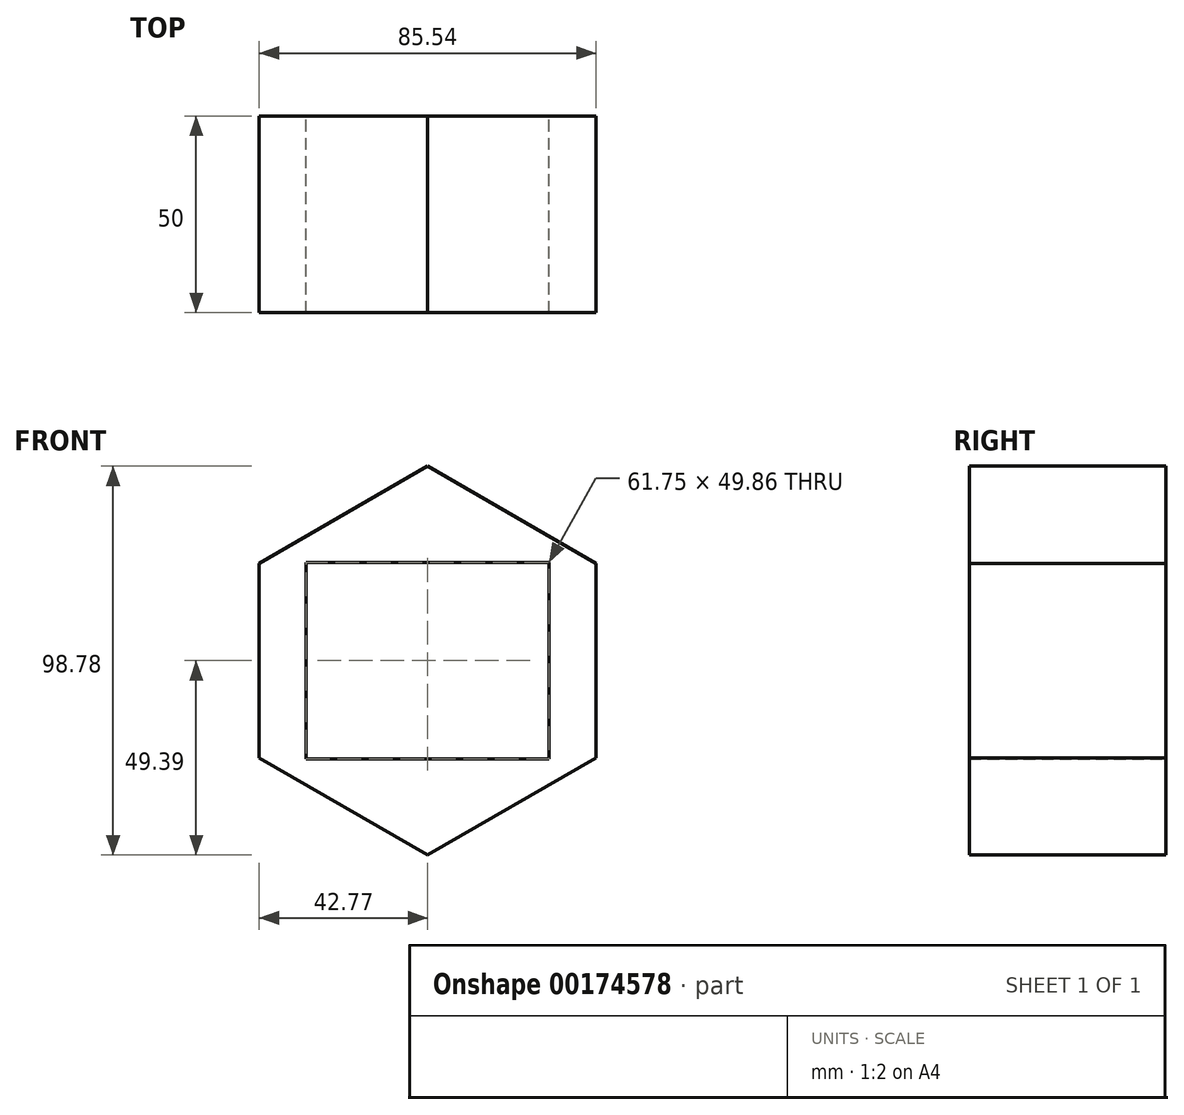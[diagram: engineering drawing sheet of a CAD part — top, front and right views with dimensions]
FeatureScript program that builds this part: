
annotation { "Feature Type Name" : "Feature", "Feature Type Description" : "" }
export const myFeature = defineFeature(function(context is Context, id is Id, definition is map)
    precondition{}
    {
        {
            var Q0;
            Q0=qCreatedBy(makeId("Front.planeOp"),FACE);
            var sketch = newSketch(context, id + "F0", { "sketchPlane" : qUnion([Q0])});
            skCircle(sketch, "E0.cCircle", {"center": v(0, 0) * mm, "radius": 42.77 * mm, "construction": true});
            skLineSegment(sketch, "E0.0", {"start": v(-42.77, -24.7) * mm, "end": v(-42.77, 24.7) * mm});
            skLineSegment(sketch, "E0.1", {"start": v(-42.77, 24.7) * mm, "end": v(0, 49.4) * mm});
            skLineSegment(sketch, "E0.2", {"start": v(0, 49.4) * mm, "end": v(42.77, 24.7) * mm});
            skLineSegment(sketch, "E0.3", {"start": v(42.77, 24.7) * mm, "end": v(42.77, -24.7) * mm});
            skLineSegment(sketch, "E0.4", {"start": v(42.77, -24.7) * mm, "end": v(0, -49.4) * mm});
            skLineSegment(sketch, "E0.5", {"start": v(0, -49.4) * mm, "end": v(-42.77, -24.7) * mm});
            skPoint(sketch, "E0.0.midPoint", {"position": v(-42.77, 0) * mm});
            skCircle(sketch, "E1", {"center": v(0, 0) * mm, "radius": 10 * mm});
            skLineSegment(sketch, "E2.bottom", {"start": v(-30.88, -24.93) * mm, "end": v(30.88, -24.93) * mm});
            skLineSegment(sketch, "E2.top", {"start": v(-30.88, 24.93) * mm, "end": v(30.88, 24.93) * mm});
            skLineSegment(sketch, "E2.left", {"start": v(-30.88, -24.93) * mm, "end": v(-30.88, 24.93) * mm});
            skLineSegment(sketch, "E2.right", {"start": v(30.88, -24.93) * mm, "end": v(30.88, 24.93) * mm});
            skArc(sketch, "E3", {"start": v(-17.56, 0) * mm, "mid": v(0, 17.56) * mm, "end": v(17.56, 0) * mm});
            skArc(sketch, "E4", {"start": v(-17.56, 0) * mm, "mid": v(0, -17.56) * mm, "end": v(17.56, 0) * mm});
            skSolve(sketch);
        }
        {
            var Q0;
            Q0=makeQuery(id+"F0.imprint","IMPRINT",FACE,{"disambiguationData":[TD([[makeQuery(id+"F0.imprint","IMPRINT",EDGE,{"derivedFrom":sQuery(id+"F0.wireOp",EDGE,"E0.0")}),-1.0]])]});
            extrude(context, id + "F1", {"entities" : qUnion([Q0]), "depth" : 50 * mm});
        }
    });
